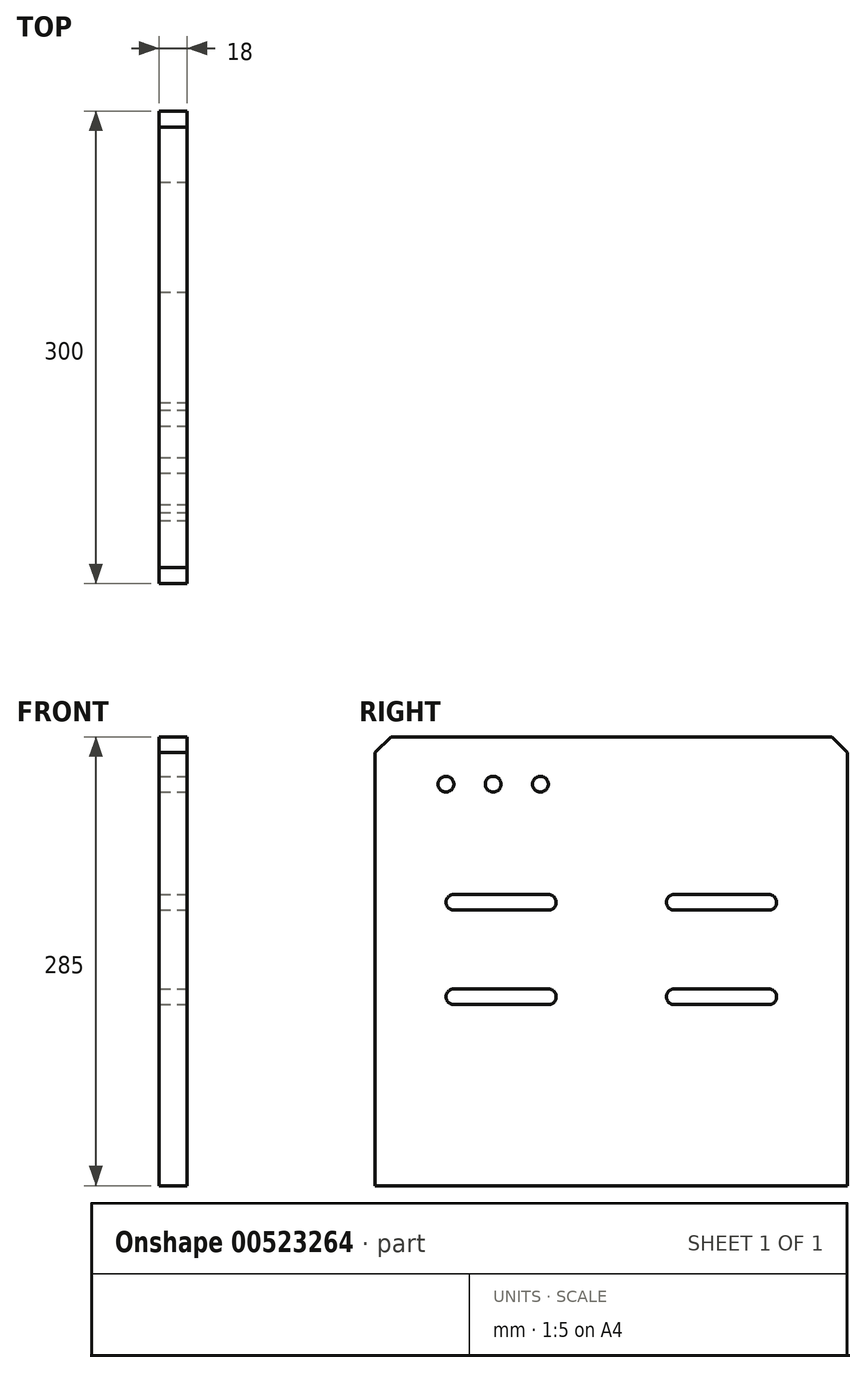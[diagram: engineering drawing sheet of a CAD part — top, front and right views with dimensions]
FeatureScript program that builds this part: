
annotation { "Feature Type Name" : "Feature", "Feature Type Description" : "" }
export const myFeature = defineFeature(function(context is Context, id is Id, definition is map)
    precondition{}
    {
        {
            var Q0;
            Q0=qCreatedBy(makeId("Right.planeOp"),FACE);
            var sketch = newSketch(context, id + "F0", { "sketchPlane" : qUnion([Q0])});
            skLineSegment(sketch, "E0.bottom", {"start": v(0, 0) * mm, "end": v(300, 0) * mm});
            skLineSegment(sketch, "E0.top", {"start": v(0, 285) * mm, "end": v(300, 285) * mm});
            skLineSegment(sketch, "E0.left", {"start": v(0, 0) * mm, "end": v(0, 285) * mm});
            skLineSegment(sketch, "E0.right", {"start": v(300, 0) * mm, "end": v(300, 285) * mm});
            skSolve(sketch);
        }
        {
            var Q0;
            Q0 = qSketchRegion(id + "F0", true);
            extrude(context, id + "F1", {"entities" : qUnion([Q0]), "depth" : 18 * mm, "offsetDistance" : 25 * mm});
        }
        {
            var Q0;
            Q0=makeQuery(id+"F1.opExtrude","CAP_FACE",FACE,{"disambiguationData":[OSD([sQuery(id+"F0.wireOp",EDGE,"E0.bottom"),sQuery(id+"F0.wireOp",EDGE,"E0.top"),sQuery(id+"F0.wireOp",EDGE,"E0.left"),sQuery(id+"F0.wireOp",EDGE,"E0.right")])],"isStart":false});
            var sketch = newSketch(context, id + "F2", { "sketchPlane" : qUnion([Q0])});
            skCircle(sketch, "E1", {"center": v(45, 255) * mm, "radius": 5 * mm});
            skCircle(sketch, "E2", {"center": v(75, 255) * mm, "radius": 5 * mm});
            skCircle(sketch, "E3", {"center": v(105, 255) * mm, "radius": 5 * mm});
            skLineSegment(sketch, "E4", {"start": v(0, 150) * mm, "end": v(300, 150) * mm, "construction": true});
            skLineSegment(sketch, "E5", {"start": v(0, 120) * mm, "end": v(300, 120) * mm, "construction": true});
            skLineSegment(sketch, "E6.MirrorCS", {"start": v(0, 180) * mm, "end": v(115, 180) * mm, "construction": true});
            skLineSegment(sketch, "E7", {"start": v(80, 125) * mm, "end": v(80, 115) * mm, "construction": true});
            skArc(sketch, "E8", {"start": v(50, 125) * mm, "mid": v(45, 120) * mm, "end": v(50, 115) * mm});
            skLineSegment(sketch, "E9", {"start": v(50, 125) * mm, "end": v(80, 125) * mm});
            skLineSegment(sketch, "E10", {"start": v(50, 115) * mm, "end": v(80, 115) * mm});
            skLineSegment(sketch, "E11.MirrorCS", {"start": v(110, 115) * mm, "end": v(80, 115) * mm});
            skLineSegment(sketch, "E12.MirrorCS", {"start": v(110, 125) * mm, "end": v(80, 125) * mm});
            skArc(sketch, "E13.MirrorCS", {"start": v(110, 125) * mm, "mid": v(115, 120) * mm, "end": v(110, 115) * mm});
            skLineSegment(sketch, "E14", {"start": v(150, 120) * mm, "end": v(150, 180) * mm, "construction": true});
            skLineSegment(sketch, "E15.MirrorCS", {"start": v(50, 175) * mm, "end": v(80, 175) * mm});
            skLineSegment(sketch, "E16.MirrorCS", {"start": v(110, 175) * mm, "end": v(80, 175) * mm});
            skArc(sketch, "E17.MirrorCS", {"start": v(110, 175) * mm, "mid": v(115, 180) * mm, "end": v(110, 185) * mm});
            skArc(sketch, "E18.MirrorCS", {"start": v(50, 175) * mm, "mid": v(45, 180) * mm, "end": v(50, 185) * mm});
            skLineSegment(sketch, "E19.MirrorCS", {"start": v(110, 185) * mm, "end": v(80, 185) * mm});
            skLineSegment(sketch, "E20.MirrorCS", {"start": v(50, 185) * mm, "end": v(80, 185) * mm});
            skLineSegment(sketch, "E21.MirrorCS", {"start": v(190, 175) * mm, "end": v(220, 175) * mm});
            skLineSegment(sketch, "E22.MirrorCS", {"start": v(250, 175) * mm, "end": v(220, 175) * mm});
            skLineSegment(sketch, "E23.MirrorCS", {"start": v(250, 185) * mm, "end": v(220, 185) * mm});
            skLineSegment(sketch, "E24.MirrorCS", {"start": v(190, 185) * mm, "end": v(220, 185) * mm});
            skLineSegment(sketch, "E25.MirrorCS", {"start": v(190, 115) * mm, "end": v(220, 115) * mm});
            skLineSegment(sketch, "E26.MirrorCS", {"start": v(250, 115) * mm, "end": v(220, 115) * mm});
            skArc(sketch, "E27.MirrorCS", {"start": v(250, 125) * mm, "mid": v(255, 120) * mm, "end": v(250, 115) * mm});
            skArc(sketch, "E28.MirrorCS", {"start": v(190, 125) * mm, "mid": v(185, 120) * mm, "end": v(190, 115) * mm});
            skLineSegment(sketch, "E29.MirrorCS", {"start": v(190, 125) * mm, "end": v(220, 125) * mm});
            skLineSegment(sketch, "E30.MirrorCS", {"start": v(250, 125) * mm, "end": v(220, 125) * mm});
            skLineSegment(sketch, "E31.MirrorCS", {"start": v(300, 180) * mm, "end": v(0, 180) * mm, "construction": true});
            skArc(sketch, "E32.MirrorCS", {"start": v(190, 175) * mm, "mid": v(185, 180) * mm, "end": v(190, 185) * mm});
            skLineSegment(sketch, "E33.trimOffspring", {"start": v(185, 180) * mm, "end": v(300, 180) * mm, "construction": true});
            skPoint(sketch, "E34.orphan", {"position": v(250, 185) * mm});
            skPoint(sketch, "E35.MirrorCS.start.orphan", {"position": v(250, 175) * mm});
            skArc(sketch, "E36.MirrorCS", {"start": v(250, 175) * mm, "mid": v(255, 180) * mm, "end": v(250, 185) * mm});
            skSolve(sketch);
        }
        {
            var Q0;
            Q0 = qSketchRegion(id + "F2", true);
            extrude(context, id + "F3", {"entities" : qUnion([Q0]), "operationType" : NewBodyOperationType.REMOVE, "endBound" : BoundingType.THROUGH_ALL, "oppositeDirection" : true, "depth" : 25 * mm, "offsetDistance" : 25 * mm});
        }
        {
            var Q0;
            Q0=makeQuery(id+"F1.opExtrude","SWEPT_EDGE",EDGE,{"disambiguationData":[OSD([sQuery(id+"F0.wireOp",EDGE,"E0.top"),sQuery(id+"F0.wireOp",EDGE,"E0.left")])]});
            var Q1;
            Q1=makeQuery(id+"F1.opExtrude","SWEPT_EDGE",EDGE,{"disambiguationData":[OSD([sQuery(id+"F0.wireOp",EDGE,"E0.top"),sQuery(id+"F0.wireOp",EDGE,"E0.right")])]});
            chamfer(context, id + "F4", {"entities" : qUnion([Q0, Q1]), "width" : 10 * mm, "tangentPropagation" : true});
        }
    });
